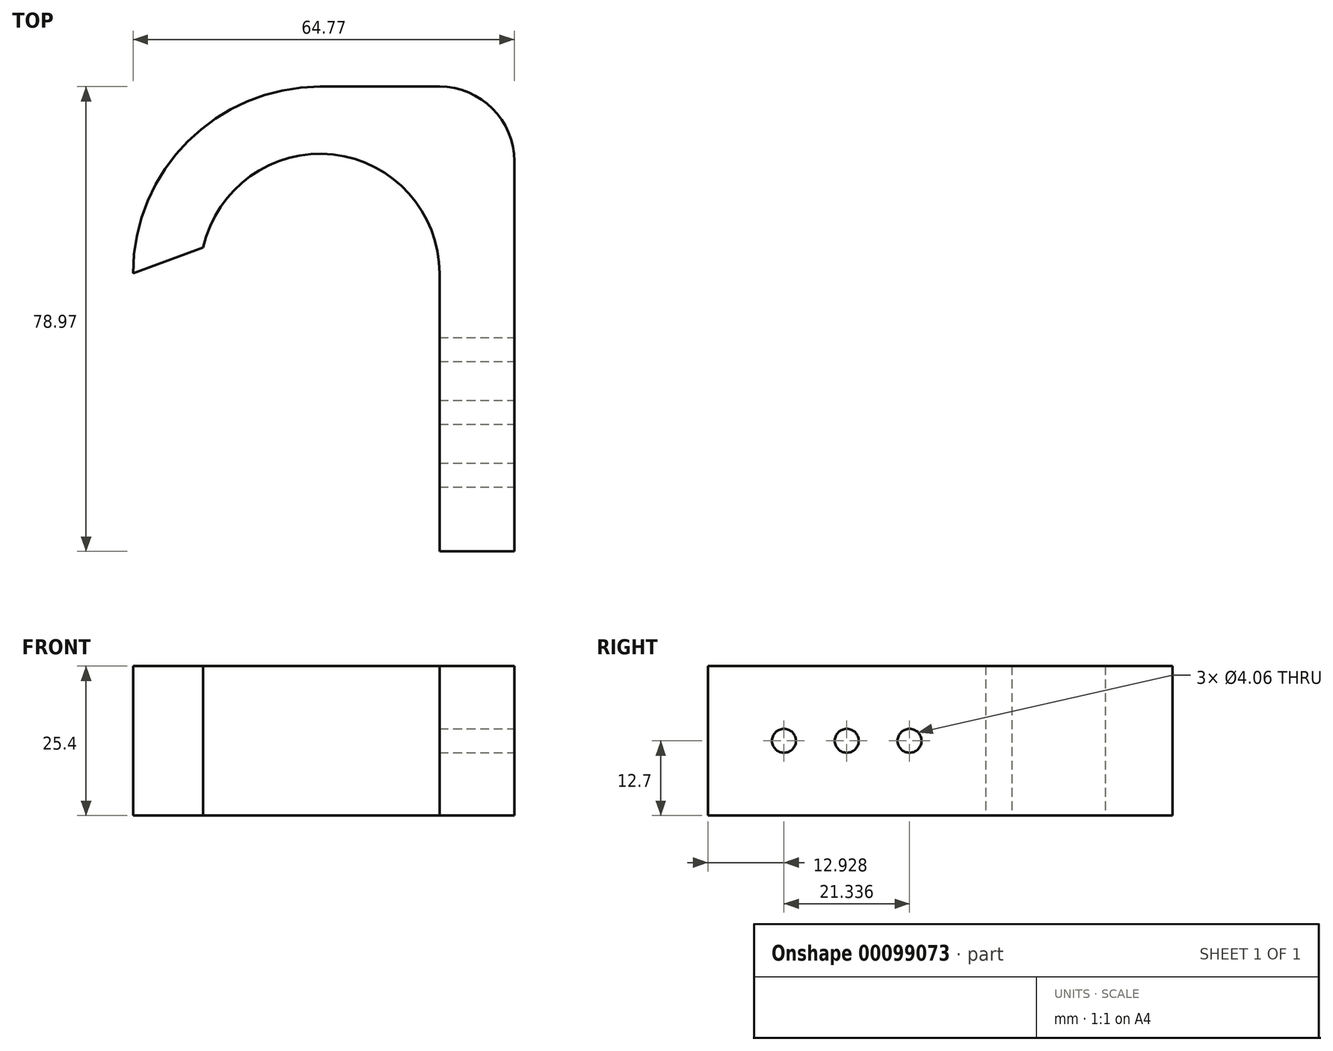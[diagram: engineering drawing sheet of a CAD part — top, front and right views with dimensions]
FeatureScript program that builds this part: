
annotation { "Feature Type Name" : "Feature", "Feature Type Description" : "" }
export const myFeature = defineFeature(function(context is Context, id is Id, definition is map)
    precondition{}
    {
        {
            var Q0;
            Q0=qCreatedBy(makeId("Top.planeOp"),FACE);
            var sketch = newSketch(context, id + "F0", { "sketchPlane" : qUnion([Q0])});
            skArc(sketch, "E0", {"start": v(20.32, 0) * mm, "mid": v(2.21, 20.2) * mm, "end": v(-19.84, 4.4) * mm});
            skArc(sketch, "E1", {"start": v(0, 31.75) * mm, "mid": v(-22.45, 22.45) * mm, "end": v(-31.75, 0) * mm});
            skLineSegment(sketch, "E2", {"start": v(-31.75, 0) * mm, "end": v(-19.84, 4.4) * mm});
            skLineSegment(sketch, "E3", {"start": v(0, 31.75) * mm, "end": v(20.32, 31.75) * mm});
            skLineSegment(sketch, "E4", {"start": v(33.02, 19.05) * mm, "end": v(33.02, -47.22) * mm});
            skLineSegment(sketch, "E5", {"start": v(33.02, -47.22) * mm, "end": v(20.32, -47.22) * mm});
            skLineSegment(sketch, "E6", {"start": v(20.32, -47.22) * mm, "end": v(20.32, 0) * mm});
            skPoint(sketch, "E7.visualSharp", {"position": v(33.02, 31.75) * mm});
            skArc(sketch, "E7.filletArc", {"start": v(33.02, 19.05) * mm, "mid": v(29.3, 28.03) * mm, "end": v(20.32, 31.75) * mm});
            skSolve(sketch);
        }
        {
            var Q0;
            Q0 = qSketchRegion(id + "F0", true);
            extrude(context, id + "F1", {"entities" : qUnion([Q0]), "depth" : 25.4 * mm});
        }
        {
            var Q0;
            Q0=makeQuery(id+"F1.opExtrude","SWEPT_FACE",FACE,{"disambiguationData":[OSD([sQuery(id+"F0.wireOp",EDGE,"E4")])]});
            var sketch = newSketch(context, id + "F2", { "sketchPlane" : qUnion([Q0])});
            skCircle(sketch, "E8", {"center": v(-34.3, 12.7) * mm, "radius": 2.03 * mm});
            skCircle(sketch, "E9", {"center": v(-23.62, 12.7) * mm, "radius": 2.03 * mm});
            skCircle(sketch, "E10", {"center": v(-12.96, 12.7) * mm, "radius": 2.03 * mm});
            skSolve(sketch);
        }
        {
            var Q0;
            Q0=makeQuery(id+"F2.imprint","IMPRINT",FACE,{"disambiguationData":[TD([[makeQuery(id+"F2.imprint","IMPRINT",EDGE,{"derivedFrom":sQuery(id+"F2.wireOp",EDGE,"E8")}),1.0]])]});
            var Q1;
            Q1=makeQuery(id+"F2.imprint","IMPRINT",FACE,{"disambiguationData":[TD([[makeQuery(id+"F2.imprint","IMPRINT",EDGE,{"derivedFrom":sQuery(id+"F2.wireOp",EDGE,"E9")}),1.0]])]});
            var Q2;
            Q2=makeQuery(id+"F2.imprint","IMPRINT",FACE,{"disambiguationData":[TD([[makeQuery(id+"F2.imprint","IMPRINT",EDGE,{"derivedFrom":sQuery(id+"F2.wireOp",EDGE,"E10")}),1.0]])]});
            extrude(context, id + "F3", {"entities" : qUnion([Q0, Q1, Q2]), "operationType" : NewBodyOperationType.REMOVE, "endBound" : BoundingType.UP_TO_NEXT, "oppositeDirection" : true, "depth" : 25.4 * mm});
        }
    });
